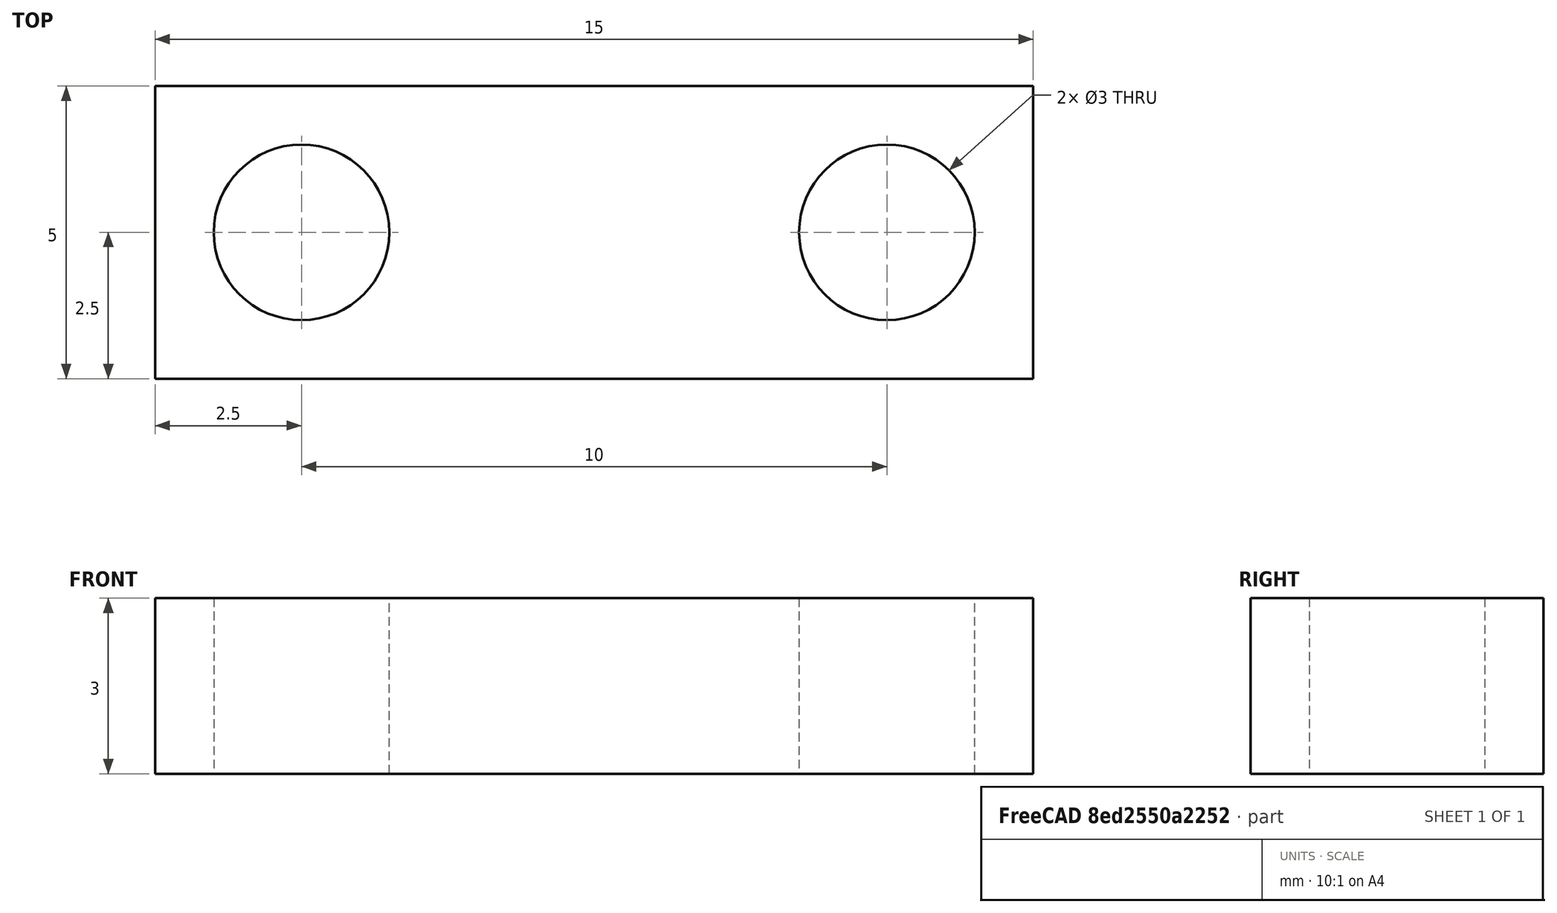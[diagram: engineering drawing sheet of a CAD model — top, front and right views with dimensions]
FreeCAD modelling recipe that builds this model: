
FCSTD DOCUMENT  (FreeCAD 0.16R6707 (Git))
Label: blocage_h
License: All rights reserved
LicenseURL: http://en.wikipedia.org/wiki/All_rights_reserved
objects: Sketcher::SketchObject×1, PartDesign::Pad×1
note: 3 computed .brp shape members not serialized (recipe doc carries the construction recipe); baked Part::Feature solids carry a one-line shape summary decoded from their .brp

FEATURE [Sketcher::SketchObject] Sketch
  sketch-geometry (8):
    g0: LineSegment StartX=0 StartY=0 StartZ=0 EndX=15 EndY=0 EndZ=0
    g1: LineSegment StartX=15 StartY=0 StartZ=0 EndX=15 EndY=5 EndZ=0
    g2: LineSegment StartX=15 StartY=5 StartZ=0 EndX=0 EndY=5 EndZ=0
    g3: LineSegment StartX=0 StartY=5 StartZ=0 EndX=0 EndY=0 EndZ=0
    g4: GeomPoint [constr] X=2.5 Y=2.5 Z=0
    g5: GeomPoint [constr] X=12.5 Y=2.5 Z=0
    g6: Circle CenterX=2.5 CenterY=2.5 CenterZ=0 NormalX=0 NormalY=0 NormalZ=1 Radius=1.5
    g7: Circle CenterX=12.5 CenterY=2.5 CenterZ=0 NormalX=0 NormalY=0 NormalZ=1 Radius=1.5
  constraints (19):
    c: Coincident(g0,g1)
    c: Coincident(g1,g2)
    c: Coincident(g2,g3)
    c: Coincident(g3,g0)
    c: Horizontal(g0)
    c: Horizontal(g2)
    c: Vertical(g1)
    c: Vertical(g3)
    c: Coincident(g0,g-1)
    c: Distance(g2) = 15
    c: Distance(g3) = 5
    c: DistanceX(g4,g5) = 10
    c: DistanceY(g4,g5) = 0
    c: DistanceY(g4) = 2.5
    c: DistanceX(g4) = 2.5
    c: Coincident(g6,g4)
    c: Coincident(g7,g5)
    c: Radius(g7) = 1.5
    c: Equal(g7,g6)
FEATURE [PartDesign::Pad] Pad
  Length = 3
  Length2 = 100
  Sketch = -> Sketch
  Type = 0
